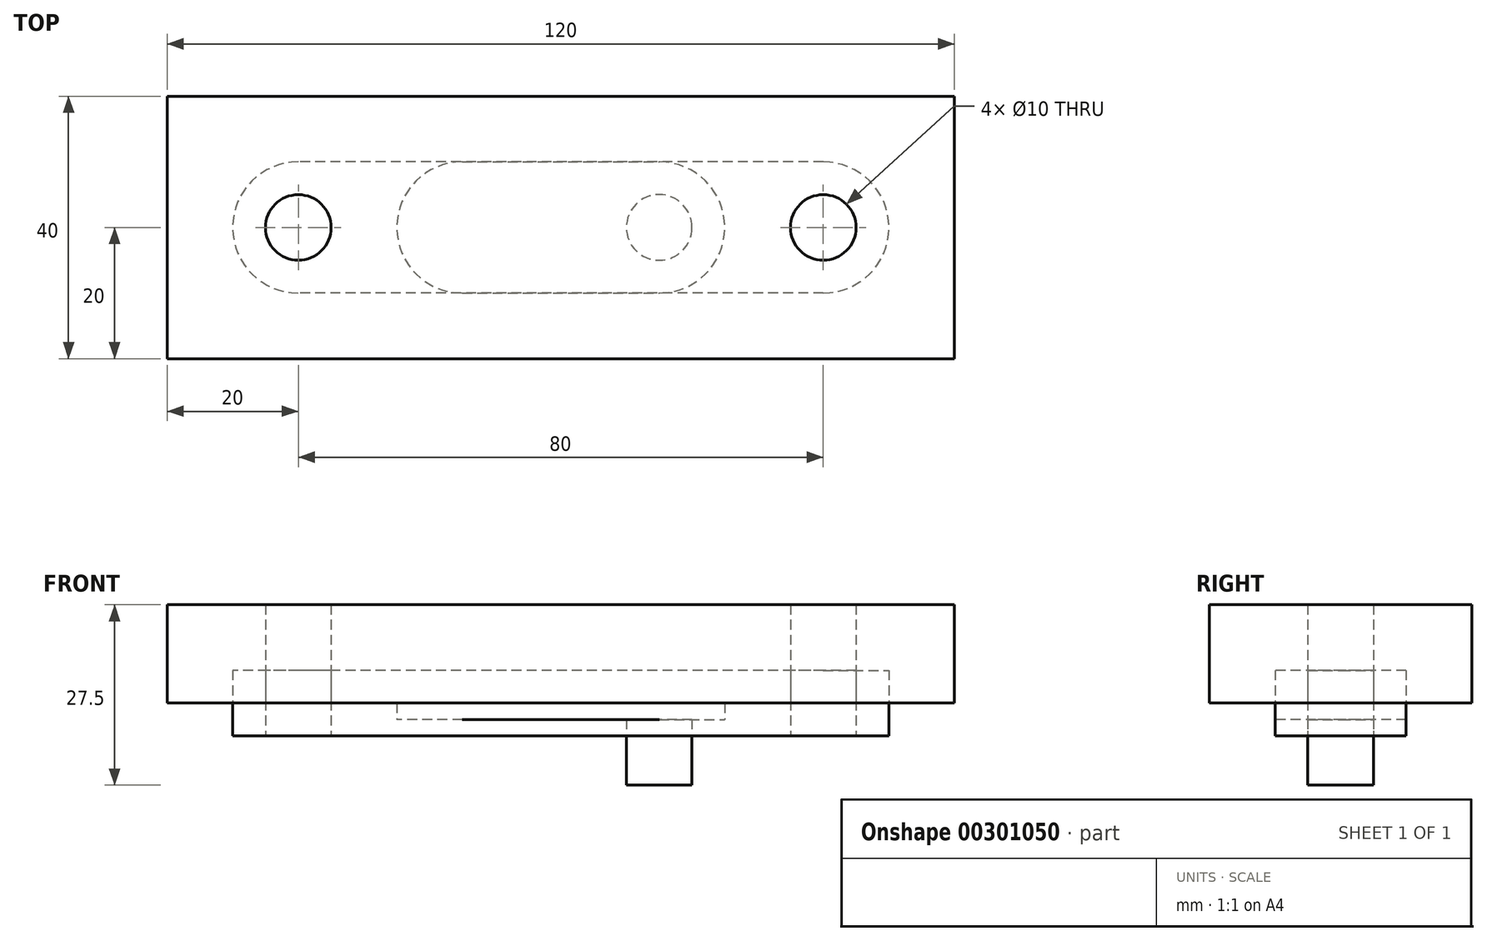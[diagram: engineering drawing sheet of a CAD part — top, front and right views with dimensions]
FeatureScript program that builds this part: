
annotation { "Feature Type Name" : "Feature", "Feature Type Description" : "" }
export const myFeature = defineFeature(function(context is Context, id is Id, definition is map)
    precondition{}
    {
        {
            var Q0;
            Q0=qCreatedBy(makeId("Top.planeOp"),FACE);
            var sketch = newSketch(context, id + "F0", { "sketchPlane" : qUnion([Q0])});
            skLineSegment(sketch, "E0.bottom", {"start": v(60, 20) * mm, "end": v(-60, 20) * mm});
            skLineSegment(sketch, "E0.top", {"start": v(60, -20) * mm, "end": v(-60, -20) * mm});
            skLineSegment(sketch, "E0.left", {"start": v(60, 20) * mm, "end": v(60, -20) * mm});
            skLineSegment(sketch, "E0.right", {"start": v(-60, 20) * mm, "end": v(-60, -20) * mm});
            skPoint(sketch, "E0.middle", {"position": v(0, 0) * mm});
            skCircle(sketch, "E1", {"center": v(-40, 0) * mm, "radius": 5 * mm});
            skCircle(sketch, "E2", {"center": v(40, 0) * mm, "radius": 5 * mm});
            skSolve(sketch);
        }
        {
            var Q0;
            Q0=makeQuery(id+"F0.imprint","IMPRINT",FACE,{"disambiguationData":[TD([[makeQuery(id+"F0.imprint","IMPRINT",EDGE,{"derivedFrom":sQuery(id+"F0.wireOp",EDGE,"E0.bottom")}),1.0]])]});
            extrude(context, id + "F1", {"entities" : qUnion([Q0]), "depth" : 15 * mm});
        }
        {
            var Q0;
            Q0=qCreatedBy(makeId("Top.planeOp"),FACE);
            var sketch = newSketch(context, id + "F2", { "sketchPlane" : qUnion([Q0])});
            skLineSegment(sketch, "E3.bottom", {"start": v(15, 10) * mm, "end": v(-15, 10) * mm});
            skLineSegment(sketch, "E3.top", {"start": v(15, -10) * mm, "end": v(-15, -10) * mm});
            skPoint(sketch, "E3.middle", {"position": v(0, 0) * mm});
            skArc(sketch, "E4", {"start": v(-15, 10) * mm, "mid": v(-25, 0) * mm, "end": v(-15, -10) * mm});
            skArc(sketch, "E5", {"start": v(15, 10) * mm, "mid": v(25, 0) * mm, "end": v(15, -10) * mm});
            skCircle(sketch, "E6", {"center": v(-15, 0) * mm, "radius": 5 * mm});
            skCircle(sketch, "E7", {"center": v(15, 0) * mm, "radius": 5 * mm});
            skSolve(sketch);
        }
        {
            var Q0;
            Q0=makeQuery(id+"F2.imprint","IMPRINT",FACE,{"disambiguationData":[TD([[makeQuery(id+"F2.imprint","IMPRINT",EDGE,{"derivedFrom":sQuery(id+"F2.wireOp",EDGE,"E3.bottom")}),1.0]])]});
            extrude(context, id + "F3", {"entities" : qUnion([Q0]), "depth" : 5 * mm, "symmetric" : true});
        }
        {
            var Q0;
            Q0=makeQuery(id+"F2.imprint","IMPRINT",FACE,{"disambiguationData":[TD([[makeQuery(id+"F2.imprint","IMPRINT",EDGE,{"derivedFrom":sQuery(id+"F2.wireOp",EDGE,"E6")}),1.0]])]});
            extrude(context, id + "F4", {"entities" : qUnion([Q0]), "operationType" : NewBodyOperationType.ADD, "depth" : 12.5 * mm, "hasSecondDirection" : true, "secondDirectionOppositeDirection" : true, "secondDirectionDepth" : 2.5 * mm});
        }
        {
            var Q0;
            Q0=makeQuery(id+"F2.imprint","IMPRINT",FACE,{"disambiguationData":[TD([[makeQuery(id+"F2.imprint","IMPRINT",EDGE,{"derivedFrom":sQuery(id+"F2.wireOp",EDGE,"E7")}),1.0]])]});
            extrude(context, id + "F5", {"entities" : qUnion([Q0]), "operationType" : NewBodyOperationType.ADD, "depth" : 2.5 * mm, "hasSecondDirection" : true, "secondDirectionOppositeDirection" : true, "secondDirectionDepth" : 12.5 * mm});
        }
        {
            var Q0;
            Q0=qCreatedBy(makeId("Top.planeOp"),FACE);
            var sketch = newSketch(context, id + "F6", { "sketchPlane" : qUnion([Q0])});
            skLineSegment(sketch, "E8.bottom", {"start": v(40, -10) * mm, "end": v(-40, -10) * mm});
            skLineSegment(sketch, "E8.top", {"start": v(40, 10) * mm, "end": v(-40, 10) * mm});
            skPoint(sketch, "E8.middle", {"position": v(0, 0) * mm});
            skArc(sketch, "E9", {"start": v(-40, 10) * mm, "mid": v(-50, 0) * mm, "end": v(-40, -10) * mm});
            skArc(sketch, "E10", {"start": v(40, 10) * mm, "mid": v(50, 0) * mm, "end": v(40, -10) * mm});
            skCircle(sketch, "E11", {"center": v(-40, 0) * mm, "radius": 5 * mm});
            skCircle(sketch, "E12", {"center": v(40, 0) * mm, "radius": 5 * mm});
            skSolve(sketch);
        }
        {
            var Q0;
            Q0=makeQuery(id+"F6.imprint","IMPRINT",FACE,{"disambiguationData":[TD([[makeQuery(id+"F6.imprint","IMPRINT",EDGE,{"derivedFrom":sQuery(id+"F6.wireOp",EDGE,"E8.bottom")}),-1.0]])]});
            extrude(context, id + "F7", {"entities" : qUnion([Q0]), "depth" : 10 * mm, "symmetric" : true});
        }
    });
